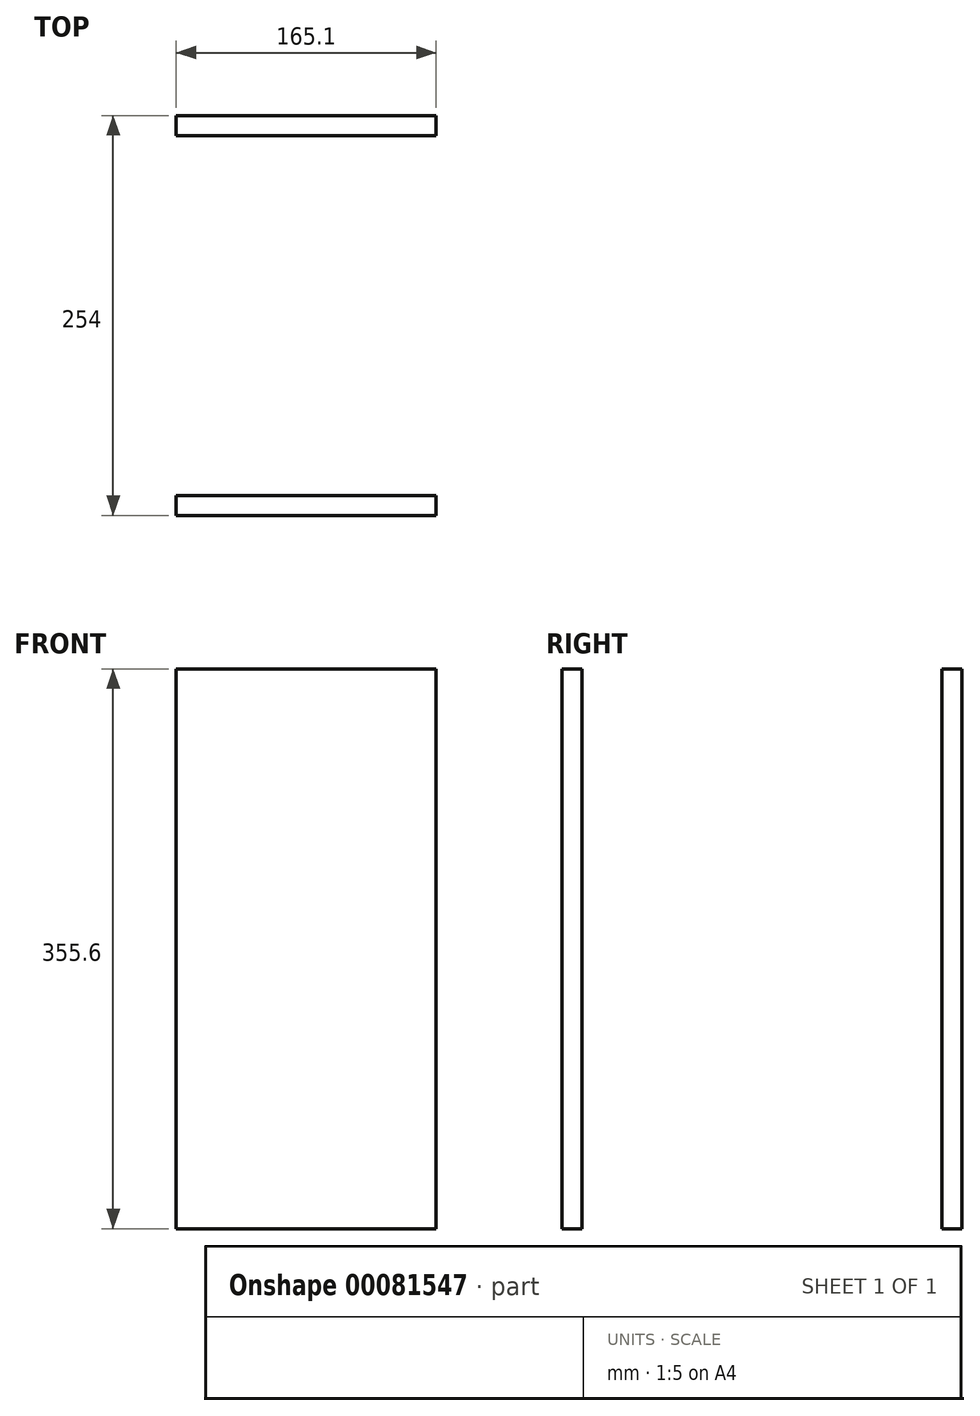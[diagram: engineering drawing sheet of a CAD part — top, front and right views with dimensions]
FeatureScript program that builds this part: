
annotation { "Feature Type Name" : "Feature", "Feature Type Description" : "" }
export const myFeature = defineFeature(function(context is Context, id is Id, definition is map)
    precondition{}
    {
        {
            var Q0;
            Q0=qCreatedBy(makeId("Front.planeOp"),FACE);
            var sketch = newSketch(context, id + "F0", { "sketchPlane" : qUnion([Q0])});
            skLineSegment(sketch, "E0.bottom", {"start": v(82.55, 177.8) * mm, "end": v(-82.55, 177.8) * mm});
            skLineSegment(sketch, "E0.top", {"start": v(82.55, -177.8) * mm, "end": v(-82.55, -177.8) * mm});
            skLineSegment(sketch, "E0.left", {"start": v(82.55, 177.8) * mm, "end": v(82.55, -177.8) * mm});
            skLineSegment(sketch, "E0.right", {"start": v(-82.55, 177.8) * mm, "end": v(-82.55, -177.8) * mm});
            skPoint(sketch, "E0.middle", {"position": v(0, 0) * mm});
            skSolve(sketch);
        }
        {
            var Q0;
            Q0 = qSketchRegion(id + "F0", true);
            extrude(context, id + "F1", {"entities" : qUnion([Q0]), "depth" : 12.7 * mm});
        }
        {
            var Q0;
            Q0=makeQuery(id+"F1.opExtrude","SWEPT_BODY",BODY,{"disambiguationData":[OSD([sQuery(id+"F0.wireOp",EDGE,"E0.bottom"),sQuery(id+"F0.wireOp",EDGE,"E0.top"),sQuery(id+"F0.wireOp",EDGE,"E0.left"),sQuery(id+"F0.wireOp",EDGE,"E0.right")])]});
            transform(context, id + "F2", {"entities" : qUnion([Q0]), "transformType" : TransformType.TRANSLATION_3D, "dx" : 0 * mm, "dy" : 241.3 * mm, "dz" : 0 * mm, "makeCopy" : true});
        }
    });
